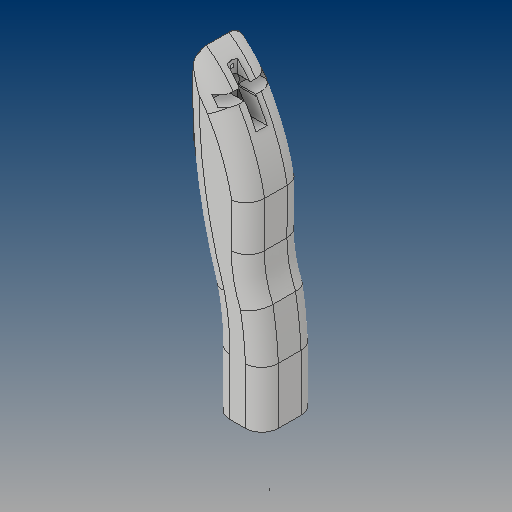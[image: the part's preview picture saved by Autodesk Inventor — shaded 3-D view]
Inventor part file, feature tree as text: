
AUTODESK INVENTOR PART (.ipt)
format: ipt  version: 2017 (Build 210142000, 142)  size: 1,043,968 bytes
history: native  units: mm
features: extrude x21, sketch x21, projected_geometry x15, fillet x2, mirror x1
ambient origin geometry x8: Origin, YZ Plane, XZ Plane, XY Plane, X Axis, Y Axis, Z Axis, Center Point
bodies: Solid1 (feature_tree)
feature tree (60):
  extrude  "Extrusion1"  Depth=35.0mm
  extrude  "Extrusion2"  Depth=9.0mm TaperAngle=0.0deg
  extrude  "Extrusion6"  Depth=70.0mm TaperAngle=0.0deg
  extrude  "Extrusion9"  TaperAngle=90.0deg  [1 undecoded]
  fillet  "Fillet1"  Radius=100.0mm
  extrude  "Extrusion10"  Depth=25.0mm TaperAngle=0.0deg
  extrude  "Extrusion11"  Depth=18.0mm TaperAngle=0.0deg
  extrude  "Extrusion12"  Depth=18.0mm TaperAngle=0.0deg
  extrude  "Extrusion13"  Depth=12.0mm
  extrude  "Extrusion14"  Depth=4.0mm TaperAngle=0.0deg
  extrude  "Extrusion15"  Depth=2.0mm
  extrude  "Extrusion16"  Depth=2.0mm
  extrude  "Extrusion17"  Depth=15.0mm TaperAngle=0.0deg
  extrude  "Extrusion18"  Depth=5.0mm
  extrude  "Extrusion19"  Depth=4.0mm TaperAngle=0.0deg
  extrude  "Extrusion20"  Depth=3.0mm
  extrude  "Extrusion21"  Depth=8.0mm
  extrude  "Extrusion22"  Depth=3.0mm
  fillet  "Fillet2"  Radius=15.0mm
  extrude  "Extrusion23"  Depth=0.1mm TaperAngle=0.0deg
  extrude  "Extrusion24"  Depth=9.0mm
  extrude  "Extrusion25"  Depth=10.0mm
  mirror  "Mirror7"
  extrude  "Extrusion26"  [1 undecoded]
  sketch  "Sketch1"  dims[d0=63.0mm d1=0.0mm d2=35.0mm]
  sketch  "Sketch3"  dims[d3=150.0mm d4=9.0mm d5=0.0mm]
  sketch  "Sketch12"  dims[d30=250.0mm d31=0.0mm d48=70.0mm d49=0.0mm]
  sketch  "Sketch17"  dims[d50=8.0mm d51=90.0deg d52=100.0mm d53=0.0mm]
  sketch  "Sketch19"  dims[d54=100.0mm d55=0.0mm d56=25.0mm d57=0.0mm]
  sketch  "Sketch20"  dims[d58=20.0mm d59=0.0mm d60=18.0mm d61=0.0mm]
  sketch  "Sketch21"  dims[d71=25.0mm d72=0.0mm d73=18.0mm d74=0.0mm]
  projected_geometry  "Projected Loop4"
  sketch  "Sketch22"  dims[d75=7.0mm d76=0.0mm d77=12.0mm]
  projected_geometry  "Projected Loop5"
  sketch  "Sketch23"  dims[d78=6.0mm d79=4.0mm d80=0.0mm]
  projected_geometry  "Projected Loop6"
  sketch  "Sketch24"  dims[d81=4.0mm d82=0.0mm d83=2.0mm]
  projected_geometry  "Projected Loop7"
  sketch  "Sketch25"  dims[d84=2.0mm d85=2.0mm]
  sketch  "Sketch26"  dims[d86=2.0mm d87=15.0mm d88=0.0mm]
  projected_geometry  "Projected Loop8"
  sketch  "Sketch27"  dims[d89=5.0mm d90=5.0mm]
  sketch  "Sketch28"  dims[d91=5.0mm d92=4.0mm d93=0.0mm]
  sketch  "Sketch30"  dims[d94=2.0mm d96=3.0mm]
  projected_geometry  "Projected Loop9"
  projected_geometry  "Projected Loop10"
  projected_geometry  "Projected Loop11"
  projected_geometry  "Projected Loop12"
  sketch  "Sketch31"  dims[d97=8.0mm d98=0.0mm d99=5.0mm]
  sketch  "Sketch32"  dims[d100=3.0mm d101=3.0mm d102=15.0mm d103=0.0mm]
  sketch  "Sketch33"  dims[d104=40.0mm d105=0.0mm d106=0.1mm d107=0.0mm]
  sketch  "Sketch34"  dims[d108=10.0mm d109=9.0mm]
  projected_geometry  "Projected Loop13"
  sketch  "Sketch35"  dims[d110=9.0mm d111=10.0mm]
  projected_geometry  "Projected Loop14"
  sketch  "Sketch38"  dims[d112=20.0mm d113=0.0mm]
  projected_geometry  "Projected Loop16"
  projected_geometry  "Projected Loop17"
  projected_geometry  "Projected Loop18"
  projected_geometry  "Projected Loop19"
note: 2 required parameter values undecoded (feature->parameter linkage not recoverable at this tier; creation-order binding heuristic only, values carry confidence <= 0.55)
